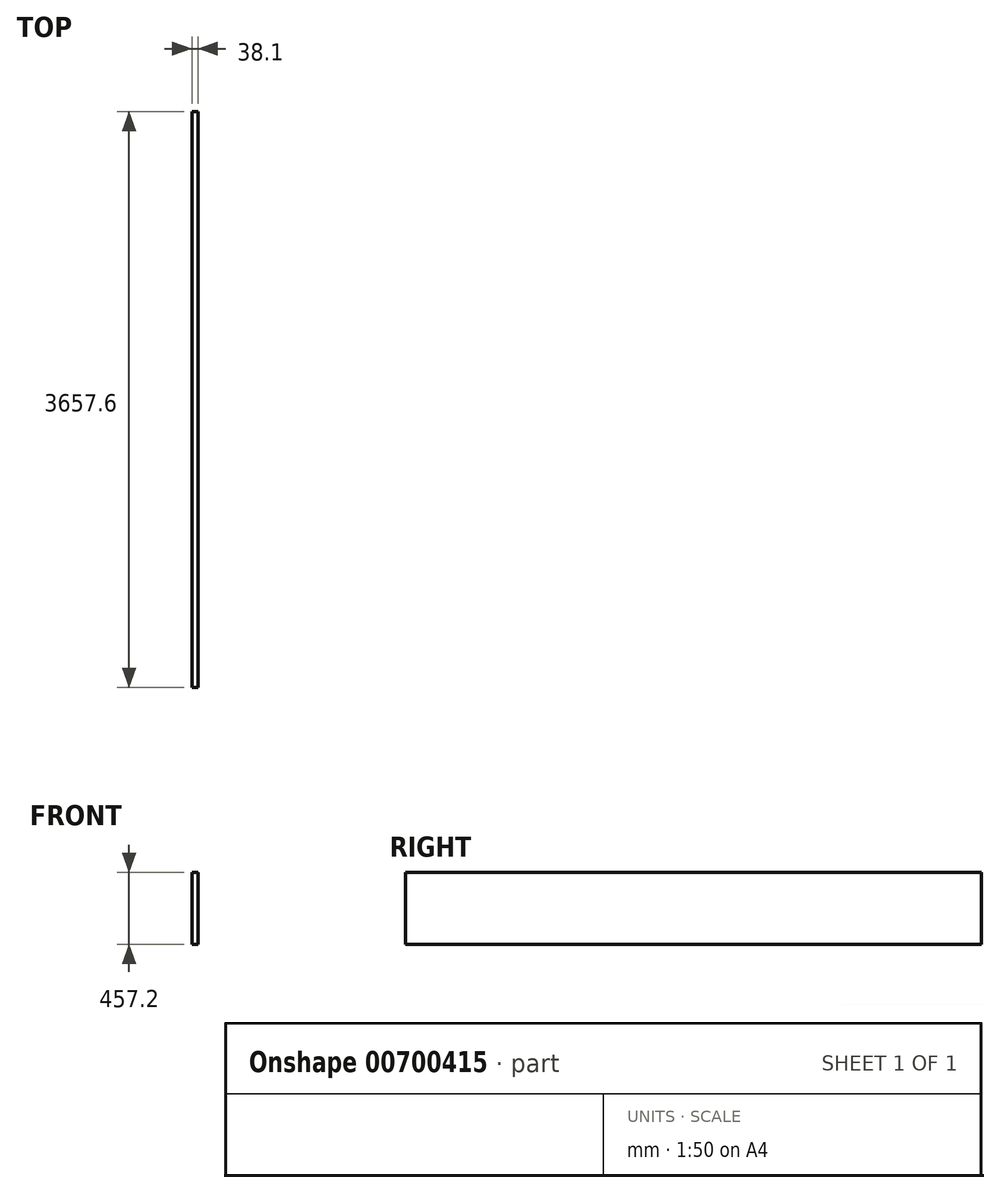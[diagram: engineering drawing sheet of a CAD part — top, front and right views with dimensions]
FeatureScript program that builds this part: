
annotation { "Feature Type Name" : "Feature", "Feature Type Description" : "" }
export const myFeature = defineFeature(function(context is Context, id is Id, definition is map)
    precondition{}
    {
        {
            var Q0;
            Q0=qCreatedBy(makeId("Front.planeOp"),FACE);
            var sketch = newSketch(context, id + "F0", { "sketchPlane" : qUnion([Q0])});
            skLineSegment(sketch, "E0.bottom", {"start": v(-19.05, 228.6) * mm, "end": v(19.05, 228.6) * mm});
            skLineSegment(sketch, "E0.top", {"start": v(-19.05, -228.6) * mm, "end": v(19.05, -228.6) * mm});
            skLineSegment(sketch, "E0.left", {"start": v(-19.05, 228.6) * mm, "end": v(-19.05, -228.6) * mm});
            skLineSegment(sketch, "E0.right", {"start": v(19.05, 228.6) * mm, "end": v(19.05, -228.6) * mm});
            skLineSegment(sketch, "E1", {"start": v(-19.05, 228.6) * mm, "end": v(19.05, -228.6) * mm, "construction": true});
            skSolve(sketch);
        }
        {
            var Q0;
            Q0=qSketchRegion(id+"F0",true);
            extrude(context, id + "F1", {"entities" : qUnion([Q0]), "endBound" : BoundingType.SYMMETRIC, "depth" : 3657.6 * mm, "offsetDistance" : 25.4 * mm});
        }
    });
